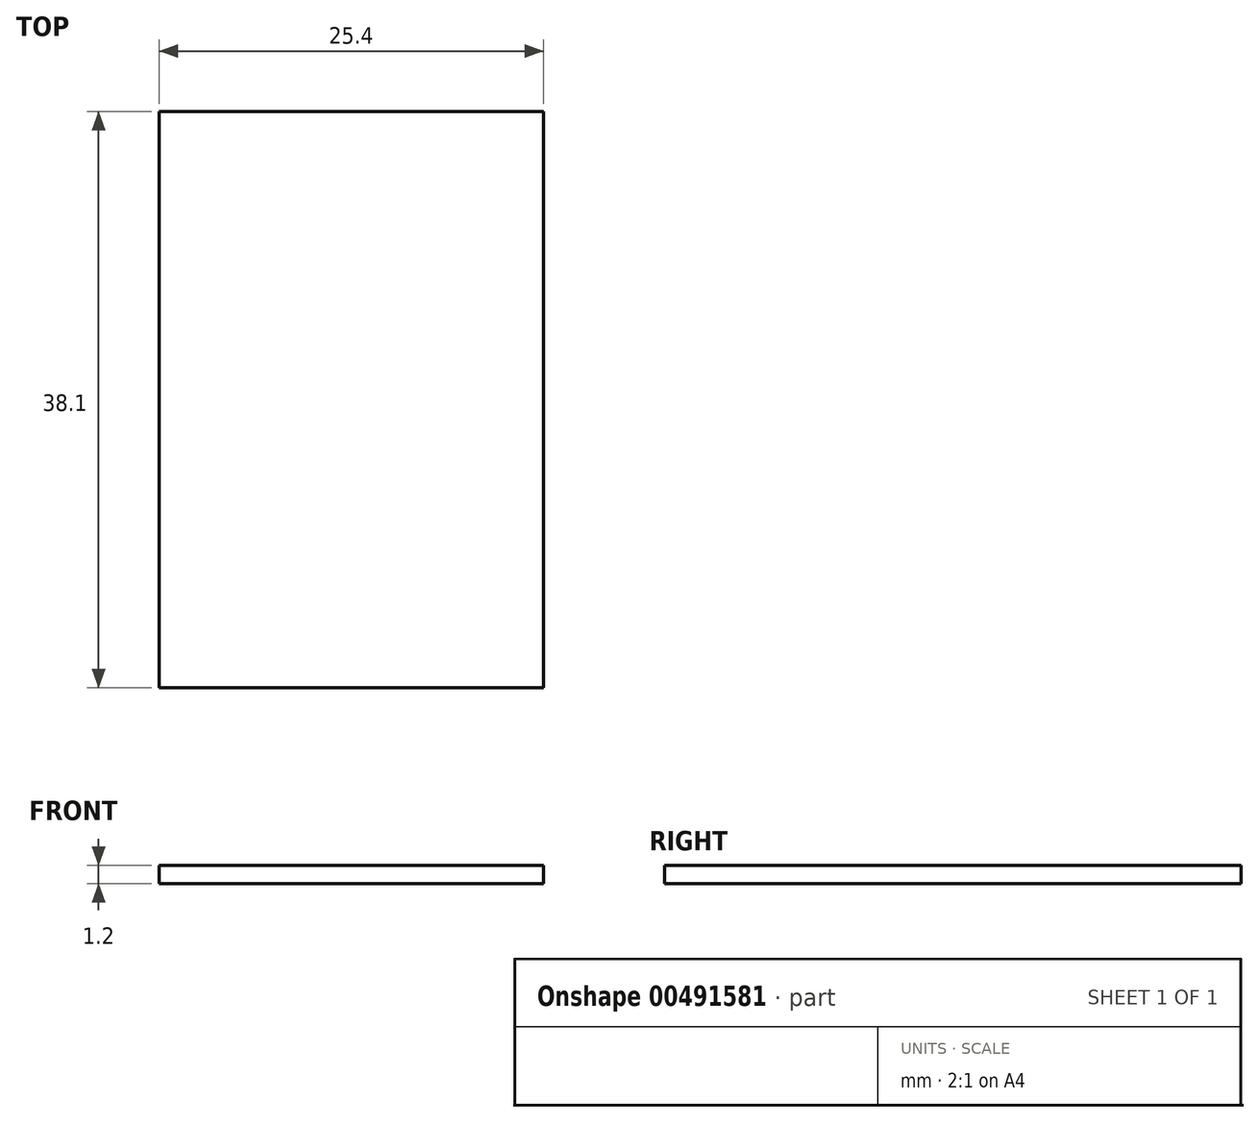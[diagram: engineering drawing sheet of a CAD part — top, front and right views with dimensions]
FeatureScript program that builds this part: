
annotation { "Feature Type Name" : "Feature", "Feature Type Description" : "" }
export const myFeature = defineFeature(function(context is Context, id is Id, definition is map)
    precondition{}
    {
        {
            var Q0;
            Q0=qCreatedBy(makeId("Top.planeOp"),FACE);
            var sketch = newSketch(context, id + "F0", { "sketchPlane" : qUnion([Q0])});
            skLineSegment(sketch, "E0.bottom", {"start": v(-12.7, 19.05) * mm, "end": v(12.7, 19.05) * mm});
            skLineSegment(sketch, "E0.top", {"start": v(-12.7, -19.05) * mm, "end": v(12.7, -19.05) * mm});
            skLineSegment(sketch, "E0.left", {"start": v(-12.7, 19.05) * mm, "end": v(-12.7, -19.05) * mm});
            skLineSegment(sketch, "E0.right", {"start": v(12.7, 19.05) * mm, "end": v(12.7, -19.05) * mm});
            skPoint(sketch, "E1", {"position": v(-12.7, 0) * mm});
            skPoint(sketch, "E2", {"position": v(0, 19.05) * mm});
            skSolve(sketch);
        }
        {
            var Q0;
            Q0=makeQuery(id+"F0.imprint","IMPRINT",FACE,{"disambiguationData":[TD([[makeQuery(id+"F0.imprint","IMPRINT",EDGE,{"derivedFrom":sQuery(id+"F0.wireOp",EDGE,"E0.bottom")}),-1.0]])]});
            extrude(context, id + "F1", {"entities" : qUnion([Q0]), "depth" : 1.2 * mm});
        }
    });
